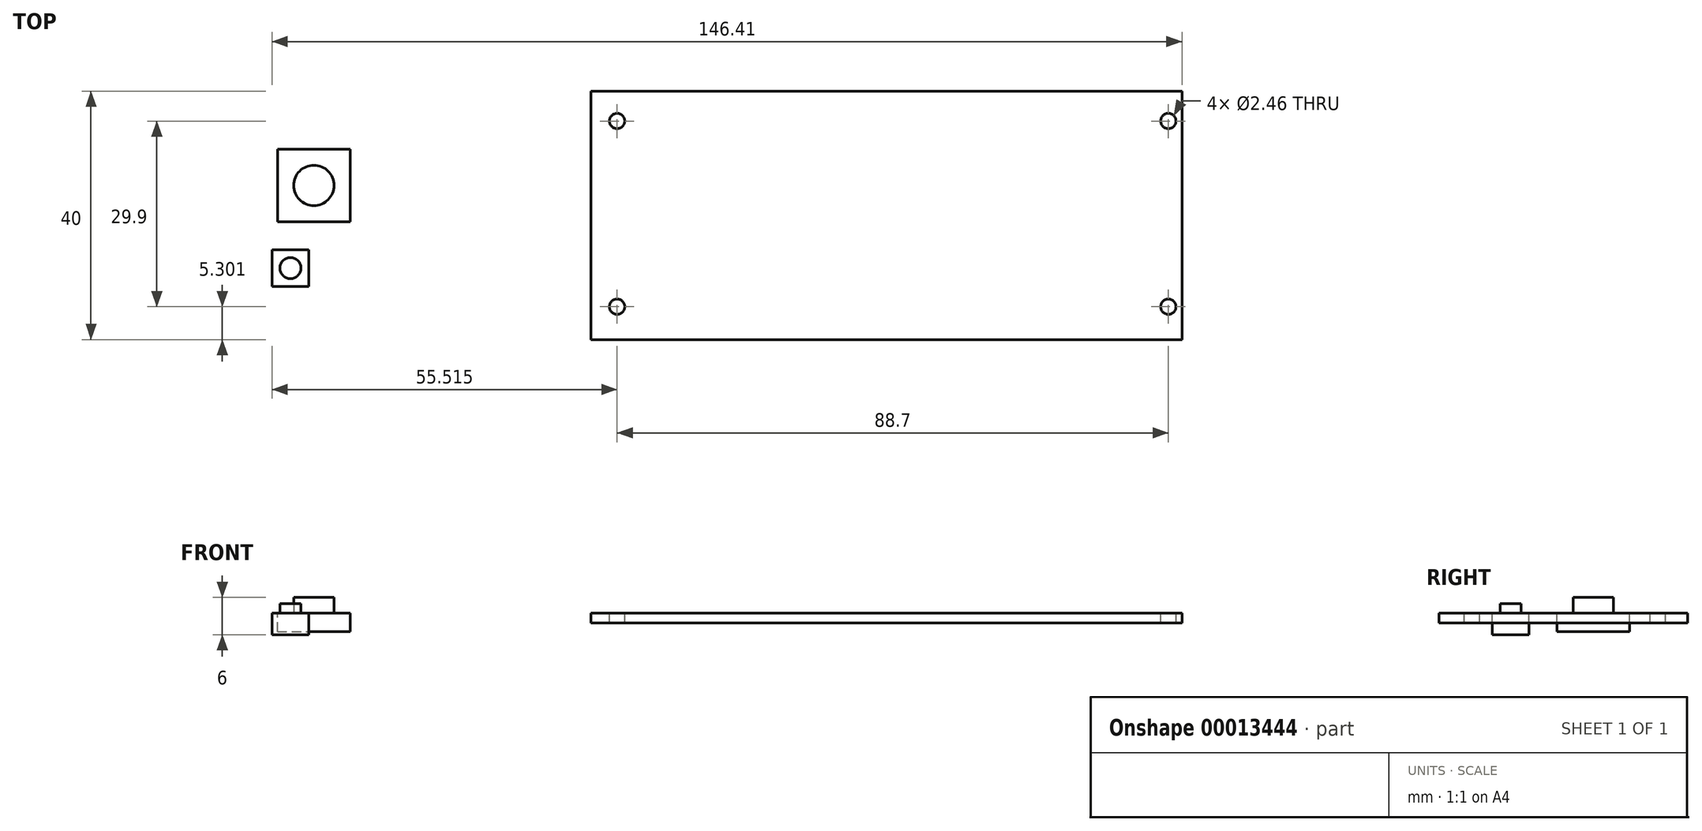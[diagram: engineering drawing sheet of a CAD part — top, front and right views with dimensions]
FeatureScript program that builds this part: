
annotation { "Feature Type Name" : "Feature", "Feature Type Description" : "" }
export const myFeature = defineFeature(function(context is Context, id is Id, definition is map)
    precondition{}
    {
        {
            var Q0;
            Q0=qCreatedBy(makeId("Top.planeOp"),FACE);
            var sketch = newSketch(context, id + "F0", { "sketchPlane" : qUnion([Q0])});
            skLineSegment(sketch, "E0.bottom", {"start": v(-45.28, 9.32) * mm, "end": v(49.82, 9.32) * mm});
            skLineSegment(sketch, "E0.top", {"start": v(-45.28, -30.68) * mm, "end": v(49.82, -30.68) * mm});
            skLineSegment(sketch, "E0.left", {"start": v(-45.28, 9.32) * mm, "end": v(-45.28, -30.68) * mm});
            skLineSegment(sketch, "E0.right", {"start": v(49.82, 9.32) * mm, "end": v(49.82, -30.68) * mm});
            skLineSegment(sketch, "E1.bottom", {"start": v(-95.72, 0) * mm, "end": v(-84.02, 0) * mm});
            skLineSegment(sketch, "E1.top", {"start": v(-95.72, -11.7) * mm, "end": v(-84.02, -11.7) * mm});
            skLineSegment(sketch, "E1.left", {"start": v(-95.72, 0) * mm, "end": v(-95.72, -11.7) * mm});
            skLineSegment(sketch, "E1.right", {"start": v(-84.02, 0) * mm, "end": v(-84.02, -11.7) * mm});
            skLineSegment(sketch, "E2", {"start": v(-95.72, 0) * mm, "end": v(-84.02, -11.7) * mm, "construction": true});
            skLineSegment(sketch, "E3", {"start": v(-84.02, 0) * mm, "end": v(-95.72, -11.7) * mm, "construction": true});
            skCircle(sketch, "E4", {"center": v(-89.87, -5.85) * mm, "radius": 3.25 * mm});
            skLineSegment(sketch, "E5.bottom", {"start": v(-96.59, -16.2) * mm, "end": v(-90.69, -16.2) * mm});
            skLineSegment(sketch, "E5.left", {"start": v(-96.59, -16.2) * mm, "end": v(-96.59, -22.1) * mm});
            skLineSegment(sketch, "E5.top", {"start": v(-96.59, -22.1) * mm, "end": v(-90.69, -22.1) * mm});
            skLineSegment(sketch, "E6", {"start": v(-96.59, -16.2) * mm, "end": v(-90.69, -22.1) * mm, "construction": true});
            skLineSegment(sketch, "E5.right", {"start": v(-90.69, -16.2) * mm, "end": v(-90.69, -22.1) * mm});
            skCircle(sketch, "E7", {"center": v(-93.64, -19.16) * mm, "radius": 1.7 * mm});
            skLineSegment(sketch, "E8", {"start": v(-90.69, -16.2) * mm, "end": v(-96.59, -22.1) * mm, "construction": true});
            skLineSegment(sketch, "E9", {"start": v(47.62, -30.68) * mm, "end": v(47.62, 9.32) * mm, "construction": true});
            skLineSegment(sketch, "E10", {"start": v(-41.08, -30.68) * mm, "end": v(-41.08, 9.32) * mm, "construction": true});
            skLineSegment(sketch, "E11", {"start": v(49.82, -25.38) * mm, "end": v(-45.28, -25.38) * mm, "construction": true});
            skLineSegment(sketch, "E12", {"start": v(49.82, 4.52) * mm, "end": v(-45.28, 4.52) * mm, "construction": true});
            skCircle(sketch, "E13", {"center": v(47.62, -25.38) * mm, "radius": 1.23 * mm});
            skCircle(sketch, "E14", {"center": v(-41.08, -25.38) * mm, "radius": 1.23 * mm});
            skCircle(sketch, "E15", {"center": v(47.62, 4.52) * mm, "radius": 1.23 * mm});
            skCircle(sketch, "E16", {"center": v(-41.08, 4.52) * mm, "radius": 1.23 * mm});
            skSolve(sketch);
        }
        {
            var Q0;
            Q0=makeQuery(id+"F0.imprint","IMPRINT",FACE,{"disambiguationData":[TD([[makeQuery(id+"F0.imprint","IMPRINT",EDGE,{"derivedFrom":sQuery(id+"F0.wireOp",EDGE,"E0.bottom")}),-1.0]])]});
            extrude(context, id + "F1", {"entities" : qUnion([Q0]), "oppositeDirection" : true, "depth" : 1.6 * mm});
        }
        {
            var Q0;
            Q0=makeQuery(id+"F1.opExtrude","CAP_FACE",FACE,{"disambiguationData":[OSD([sQuery(id+"F0.wireOp",EDGE,"E0.bottom"),sQuery(id+"F0.wireOp",EDGE,"E0.top"),sQuery(id+"F0.wireOp",EDGE,"E0.left"),sQuery(id+"F0.wireOp",EDGE,"E0.right"),sQuery(id+"F0.wireOp",EDGE,"E13"),sQuery(id+"F0.wireOp",EDGE,"E14"),sQuery(id+"F0.wireOp",EDGE,"E15"),sQuery(id+"F0.wireOp",EDGE,"E16")])],"isStart":true});
            var sketch = newSketch(context, id + "F2", { "sketchPlane" : qUnion([Q0])});
            skLineSegment(sketch, "E17.0", {"start": v(-45.28, -10.68) * mm, "end": v(49.82, -10.68) * mm, "construction": true});
            skLineSegment(sketch, "E18.0", {"start": v(-39.28, 9.32) * mm, "end": v(-39.28, -30.68) * mm, "construction": true});
            skLineSegment(sketch, "E19.0", {"start": v(-27.48, 9.32) * mm, "end": v(-27.48, -30.68) * mm, "construction": true});
            skLineSegment(sketch, "E20.0", {"start": v(-16.28, 9.32) * mm, "end": v(-16.28, -30.68) * mm, "construction": true});
            skPoint(sketch, "E21", {"position": v(-39.28, -10.68) * mm});
            skPoint(sketch, "E22", {"position": v(-16.28, -10.68) * mm});
            skLineSegment(sketch, "E23.0", {"start": v(31.12, 9.32) * mm, "end": v(31.12, -30.68) * mm, "construction": true});
            skLineSegment(sketch, "E24.0", {"start": v(19.02, 9.32) * mm, "end": v(19.02, -30.68) * mm, "construction": true});
            skLineSegment(sketch, "E25.0", {"start": v(4.22, 9.32) * mm, "end": v(4.22, -30.68) * mm, "construction": true});
            skLineSegment(sketch, "E26.0", {"start": v(-7.78, 9.32) * mm, "end": v(-7.78, -30.68) * mm, "construction": true});
            skLineSegment(sketch, "E27.0", {"start": v(-45.28, -26.18) * mm, "end": v(49.82, -26.18) * mm, "construction": true});
            skPoint(sketch, "E28", {"position": v(19.02, -10.68) * mm});
            skPoint(sketch, "E29", {"position": v(42.42, -10.68) * mm});
            skPoint(sketch, "E30", {"position": v(4.22, -26.18) * mm});
            skPoint(sketch, "E31", {"position": v(-7.78, -26.18) * mm});
            skLineSegment(sketch, "E32.0", {"start": v(-45.28, -22.08) * mm, "end": v(49.82, -22.08) * mm, "construction": true});
            skLineSegment(sketch, "E33.0", {"start": v(-45.28, 0.52) * mm, "end": v(49.82, 0.52) * mm, "construction": true});
            skPoint(sketch, "E34", {"position": v(-27.48, 0.52) * mm});
            skPoint(sketch, "E35", {"position": v(-27.48, -22.08) * mm});
            skPoint(sketch, "E36", {"position": v(31.12, -22.08) * mm});
            skPoint(sketch, "E37", {"position": v(31.12, 0.52) * mm});
            skLineSegment(sketch, "E38.0", {"start": v(42.42, 9.32) * mm, "end": v(42.42, -30.68) * mm, "construction": true});
            skSolve(sketch);
        }
        {
            var Q0;
            Q0=makeQuery(id+"F0.imprint","IMPRINT",FACE,{"disambiguationData":[TD([[makeQuery(id+"F0.imprint","IMPRINT",EDGE,{"derivedFrom":sQuery(id+"F0.wireOp",EDGE,"E1.bottom")}),-1.0]])]});
            var Q1;
            Q1=makeQuery(id+"F0.imprint","IMPRINT",FACE,{"disambiguationData":[TD([[makeQuery(id+"F0.imprint","IMPRINT",EDGE,{"derivedFrom":sQuery(id+"F0.wireOp",EDGE,"E4")}),1.0]])]});
            extrude(context, id + "F3", {"entities" : qUnion([Q0, Q1]), "oppositeDirection" : true, "depth" : 3 * mm});
        }
        {
            var Q0;
            Q0=makeQuery(id+"F0.imprint","IMPRINT",FACE,{"disambiguationData":[TD([[makeQuery(id+"F0.imprint","IMPRINT",EDGE,{"derivedFrom":sQuery(id+"F0.wireOp",EDGE,"E5.bottom")}),-1.0]])]});
            var Q1;
            Q1=makeQuery(id+"F0.imprint","IMPRINT",FACE,{"disambiguationData":[TD([[makeQuery(id+"F0.imprint","IMPRINT",EDGE,{"derivedFrom":sQuery(id+"F0.wireOp",EDGE,"E7")}),1.0]])]});
            extrude(context, id + "F4", {"entities" : qUnion([Q0, Q1]), "oppositeDirection" : true, "depth" : 3.5 * mm});
        }
        {
            var Q0;
            Q0=makeQuery(id+"F0.imprint","IMPRINT",FACE,{"disambiguationData":[TD([[makeQuery(id+"F0.imprint","IMPRINT",EDGE,{"derivedFrom":sQuery(id+"F0.wireOp",EDGE,"E7")}),1.0]])]});
            var Q1;
            Q1=sQuery(id+"F0.wireOp",EDGE,"E7");
            extrude(context, id + "F5", {"entities" : qUnion([Q0]), "operationType" : NewBodyOperationType.ADD, "surfaceEntities" : qUnion([Q1]), "depth" : 1.5 * mm});
        }
        {
            var Q0;
            Q0=makeQuery(id+"F0.imprint","IMPRINT",FACE,{"disambiguationData":[TD([[makeQuery(id+"F0.imprint","IMPRINT",EDGE,{"derivedFrom":sQuery(id+"F0.wireOp",EDGE,"E4")}),1.0]])]});
            extrude(context, id + "F6", {"entities" : qUnion([Q0]), "operationType" : NewBodyOperationType.ADD, "depth" : 2.5 * mm});
        }
    });
